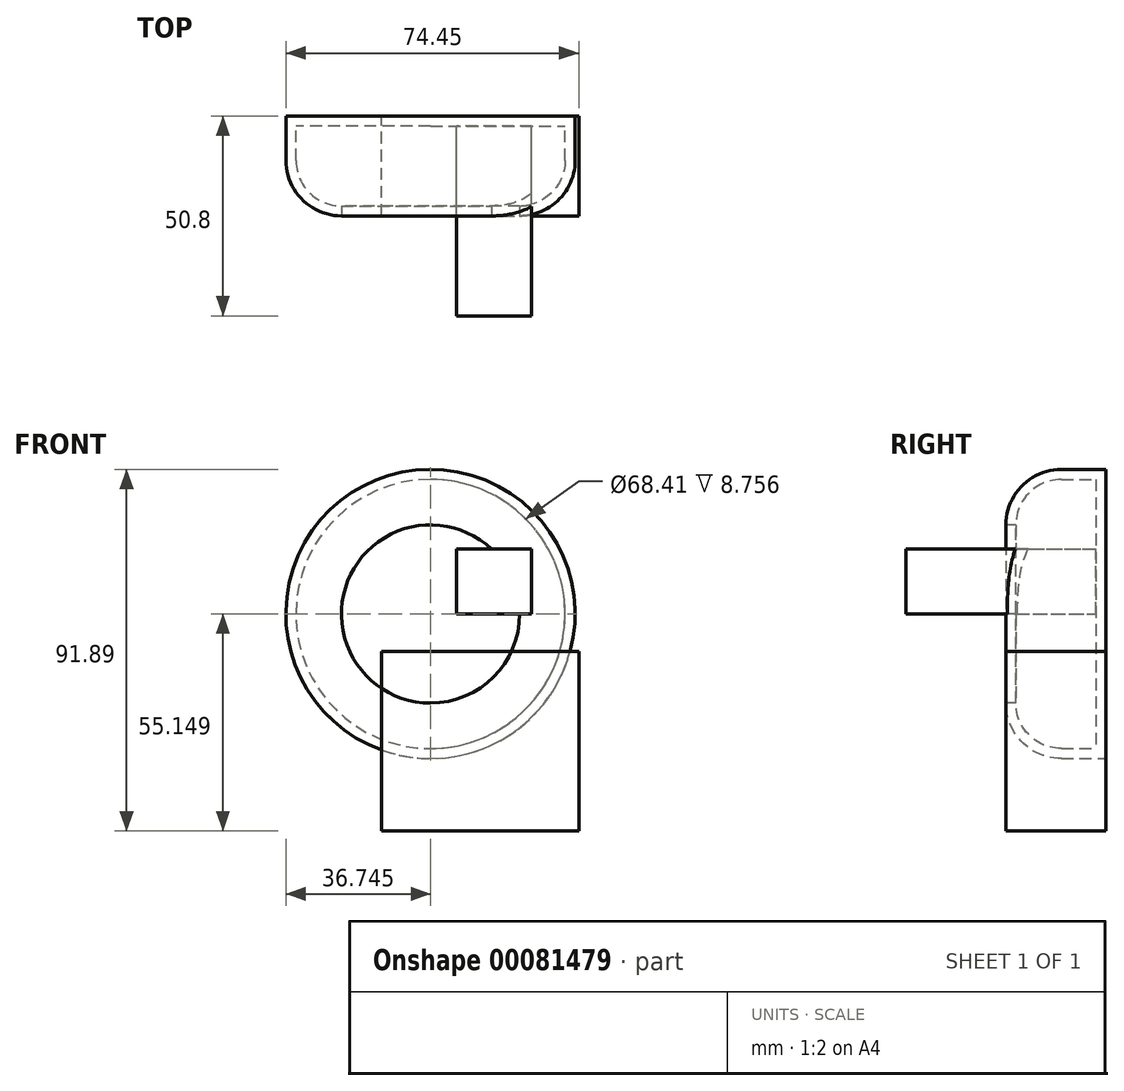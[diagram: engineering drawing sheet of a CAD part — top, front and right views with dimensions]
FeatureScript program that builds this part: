
annotation { "Feature Type Name" : "Feature", "Feature Type Description" : "" }
export const myFeature = defineFeature(function(context is Context, id is Id, definition is map)
    precondition{}
    {
        {
            var Q0;
            Q0=qCreatedBy(makeId("Front.planeOp"),FACE);
            var sketch = newSketch(context, id + "F0", { "sketchPlane" : qUnion([Q0])});
            skCircle(sketch, "E0", {"center": v(-43.33, 48.87) * mm, "radius": 36.74 * mm});
            skSolve(sketch);
        }
        {
            var Q0;
            Q0=qCreatedBy(makeId("Front.planeOp"),FACE);
            var sketch = newSketch(context, id + "F1", { "sketchPlane" : qUnion([Q0])});
            skLineSegment(sketch, "E1.bottom", {"start": v(-5.63, -6.28) * mm, "end": v(-55.72, -6.28) * mm});
            skLineSegment(sketch, "E1.top", {"start": v(-5.63, 39.3) * mm, "end": v(-55.72, 39.3) * mm});
            skLineSegment(sketch, "E1.left", {"start": v(-5.63, -6.28) * mm, "end": v(-5.63, 39.3) * mm});
            skLineSegment(sketch, "E1.right", {"start": v(-55.72, -6.28) * mm, "end": v(-55.72, 39.3) * mm});
            skLineSegment(sketch, "E2.bottom", {"start": v(-36.77, 65.38) * mm, "end": v(-17.63, 65.38) * mm});
            skLineSegment(sketch, "E2.top", {"start": v(-36.77, 48.87) * mm, "end": v(-17.63, 48.87) * mm});
            skLineSegment(sketch, "E2.left", {"start": v(-36.77, 65.38) * mm, "end": v(-36.77, 48.87) * mm});
            skLineSegment(sketch, "E2.right", {"start": v(-17.63, 65.38) * mm, "end": v(-17.63, 48.87) * mm});
            skSolve(sketch);
        }
        {
            var Q0;
            Q0=makeQuery(id+"F1.imprint","IMPRINT",FACE,{"disambiguationData":[TD([[makeQuery(id+"F1.imprint","IMPRINT",EDGE,{"derivedFrom":sQuery(id+"F1.wireOp",EDGE,"E2.bottom")}),-1.0]])]});
            var Q1;
            Q1=makeQuery(id+"F0.imprint","IMPRINT",FACE,{"disambiguationData":[TD([[makeQuery(id+"F0.imprint","IMPRINT",EDGE,{"derivedFrom":sQuery(id+"F0.wireOp",EDGE,"E0")}),1.0]])]});
            var Q2;
            Q2=makeQuery(id+"F1.imprint","IMPRINT",FACE,{"disambiguationData":[TD([[makeQuery(id+"F1.imprint","IMPRINT",EDGE,{"derivedFrom":sQuery(id+"F1.wireOp",EDGE,"E1.bottom")}),-1.0]])]});
            extrude(context, id + "F2", {"entities" : qUnion([Q0, Q1, Q2]), "depth" : 25.4 * mm});
        }
        {
            var Q0;
            Q0=makeQuery(id+"F2.opExtrude","CAP_EDGE",EDGE,{"disambiguationData":[OSD([sQuery(id+"F0.wireOp",EDGE,"E0")])],"isStart":false});
            fillet(context, id + "F3", {"entities" : qUnion([Q0]), "radius" : 14.1 * mm, "tangentPropagation" : true, "allowEdgeOverflow" : false});
        }
        {
            var Q0;
            Q0=makeQuery(id+"F2.opExtrude","CAP_FACE",FACE,{"disambiguationData":[OSD([sQuery(id+"F0.wireOp",EDGE,"E0")])],"isStart":false});
            shell(context, id + "F4", {"entities" : qUnion([Q0]), "thickness" : 2.54 * mm});
        }
        {
            var Q0;
            Q0=makeQuery(id+"F2.opExtrude","CAP_FACE",FACE,{"disambiguationData":[OSD([sQuery(id+"F1.wireOp",EDGE,"E2.bottom"),sQuery(id+"F1.wireOp",EDGE,"E2.top"),sQuery(id+"F1.wireOp",EDGE,"E2.left"),sQuery(id+"F1.wireOp",EDGE,"E2.right")])],"isStart":false});
            extrude(context, id + "F5", {"entities" : qUnion([Q0]), "operationType" : NewBodyOperationType.ADD, "depth" : 25.4 * mm});
        }
    });
